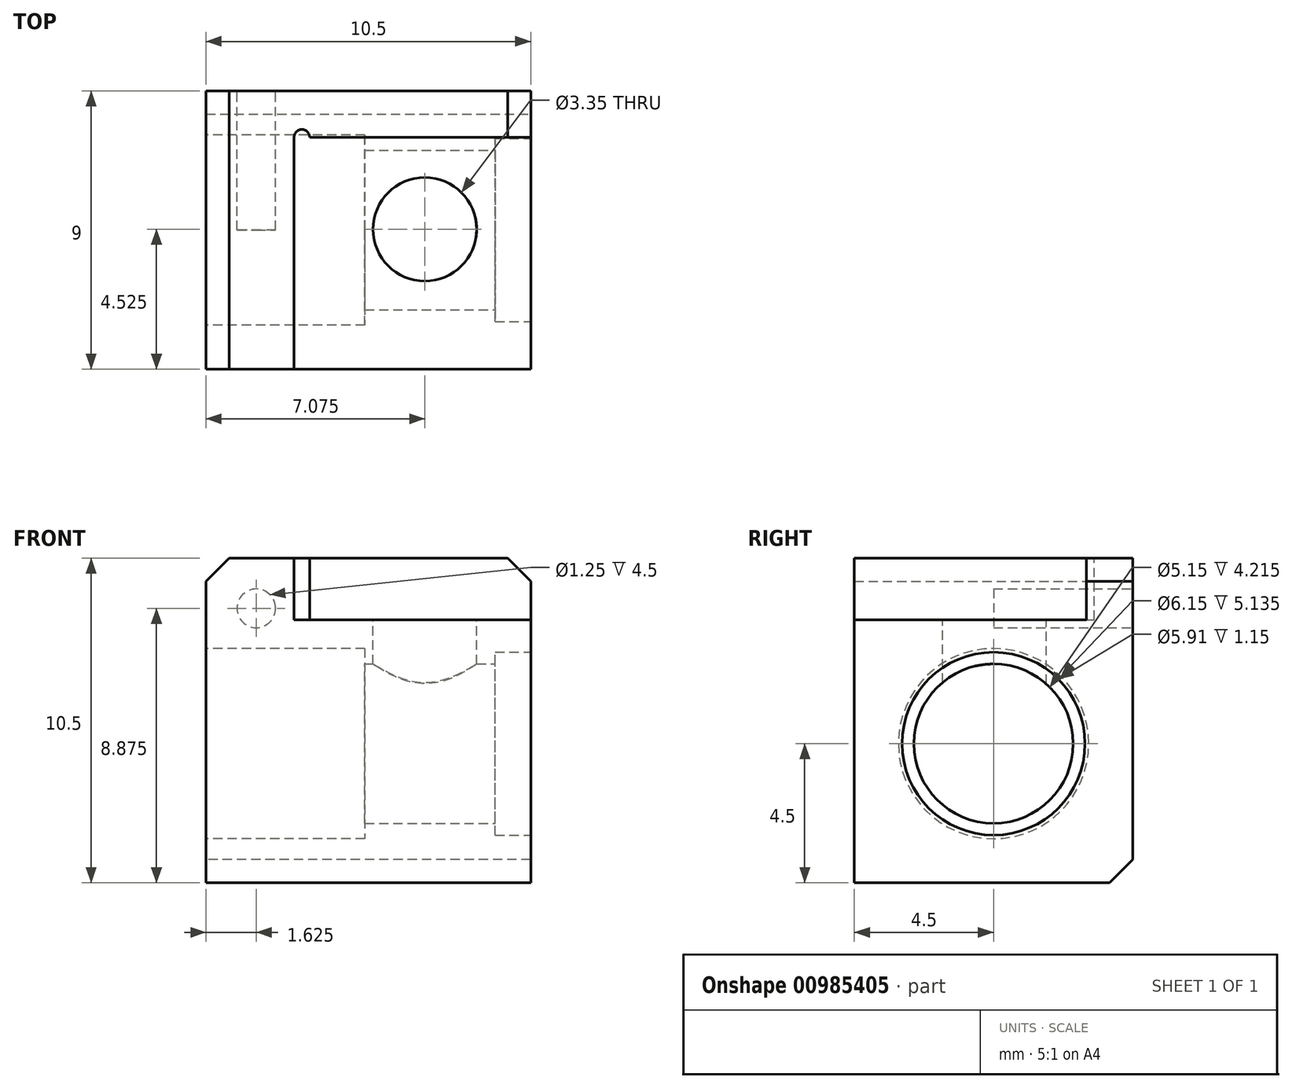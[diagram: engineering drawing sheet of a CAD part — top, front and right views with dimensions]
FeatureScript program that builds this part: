
annotation { "Feature Type Name" : "Feature", "Feature Type Description" : "" }
export const myFeature = defineFeature(function(context is Context, id is Id, definition is map)
    precondition{}
    {
        {
            var Q0;
            Q0=qCreatedBy(makeId("Front.planeOp"),FACE);
            var sketch = newSketch(context, id + "F0", { "sketchPlane" : qUnion([Q0])});
            skLineSegment(sketch, "E0.bottom", {"start": v(0, 0) * mm, "end": v(10.5, 0) * mm});
            skLineSegment(sketch, "E0.top", {"start": v(0, 10.5) * mm, "end": v(10.5, 10.5) * mm});
            skLineSegment(sketch, "E0.left", {"start": v(0, 0) * mm, "end": v(0, 10.5) * mm});
            skLineSegment(sketch, "E0.right", {"start": v(10.5, 0) * mm, "end": v(10.5, 10.5) * mm});
            skSolve(sketch);
        }
        {
            var Q0;
            Q0 = qSketchRegion(id + "F0", true);
            extrude(context, id + "F1", {"entities" : qUnion([Q0]), "depth" : 9 * mm, "offsetDistance" : 25.4 * mm});
        }
        {
            var Q0;
            Q0=makeQuery(id+"F1.opExtrude","SWEPT_FACE",FACE,{"disambiguationData":[OSD([sQuery(id+"F0.wireOp",EDGE,"E0.left")])]});
            var sketch = newSketch(context, id + "F2", { "sketchPlane" : qUnion([Q0])});
            skCircle(sketch, "E1", {"center": v(4.5, 4.5) * mm, "radius": 3.08 * mm});
            skPoint(sketch, "E1.centerSnap0", {"position": v(4.5, 0) * mm});
            skSolve(sketch);
        }
        {
            var Q0;
            Q0=makeQuery(id+"F2.imprint","IMPRINT",FACE,{"disambiguationData":[TD([[makeQuery(id+"F2.imprint","IMPRINT",EDGE,{"derivedFrom":sQuery(id+"F2.wireOp",EDGE,"E1")}),1.0]])]});
            extrude(context, id + "F3", {"entities" : qUnion([Q0]), "operationType" : NewBodyOperationType.REMOVE, "oppositeDirection" : true, "depth" : 5.13 * mm, "offsetDistance" : 25.4 * mm});
        }
        {
            var Q0;
            Q0=makeQuery(id+"F1.opExtrude","SWEPT_FACE",FACE,{"disambiguationData":[OSD([sQuery(id+"F0.wireOp",EDGE,"E0.right")])]});
            var sketch = newSketch(context, id + "F4", { "sketchPlane" : qUnion([Q0])});
            skCircle(sketch, "E2", {"center": v(-4.5, 4.5) * mm, "radius": 2.58 * mm});
            skPoint(sketch, "E2.centerSnap0", {"position": v(-4.5, 0) * mm});
            skSolve(sketch);
        }
        {
            var Q0;
            Q0 = qSketchRegion(id + "F4", true);
            extrude(context, id + "F5", {"entities" : qUnion([Q0]), "operationType" : NewBodyOperationType.REMOVE, "oppositeDirection" : true, "depth" : 25.4 * mm, "offsetDistance" : 25.4 * mm});
        }
        {
            var Q0;
            Q0=makeQuery(id+"F1.opExtrude","SWEPT_FACE",FACE,{"disambiguationData":[OSD([sQuery(id+"F0.wireOp",EDGE,"E0.top")])]});
            var sketch = newSketch(context, id + "F6", { "sketchPlane" : qUnion([Q0])});
            skLineSegment(sketch, "E3.bottom", {"start": v(10.5, -9) * mm, "end": v(2.85, -9) * mm});
            skLineSegment(sketch, "E3.top", {"start": v(10.5, -1.5) * mm, "end": v(2.85, -1.5) * mm});
            skLineSegment(sketch, "E3.left", {"start": v(10.5, -9) * mm, "end": v(10.5, -1.5) * mm});
            skLineSegment(sketch, "E3.right", {"start": v(2.85, -9) * mm, "end": v(2.85, -1.5) * mm});
            skCircle(sketch, "E4", {"center": v(3.1, -1.5) * mm, "radius": 0.25 * mm});
            skSolve(sketch);
        }
        {
            var Q0;
            Q0 = qSketchRegion(id + "F6", true);
            extrude(context, id + "F7", {"entities" : qUnion([Q0]), "operationType" : NewBodyOperationType.REMOVE, "oppositeDirection" : true, "depth" : 2 * mm, "offsetDistance" : 25.4 * mm});
        }
        {
            var Q0;
            Q0=makeQuery(id+"F7.boolean.opBoolean","COPY",FACE,{"derivedFrom":makeQuery(id+"F7.opExtrude","CAP_FACE",FACE,{"disambiguationData":[OSD([sQuery(id+"F6.wireOp",EDGE,"E3.bottom"),sQuery(id+"F6.wireOp",EDGE,"E3.top"),sQuery(id+"F6.wireOp",EDGE,"E3.left"),sQuery(id+"F6.wireOp",EDGE,"E3.right"),sQuery(id+"F6.wireOp",EDGE,"E4")])],"isStart":false})});
            var sketch = newSketch(context, id + "F8", { "sketchPlane" : qUnion([Q0])});
            skCircle(sketch, "E5", {"center": v(7.08, -4.48) * mm, "radius": 1.68 * mm});
            skSolve(sketch);
        }
        {
            var Q0;
            Q0 = qSketchRegion(id + "F8", true);
            extrude(context, id + "F9", {"entities" : qUnion([Q0]), "operationType" : NewBodyOperationType.REMOVE, "oppositeDirection" : true, "depth" : 3 * mm, "offsetDistance" : 25.4 * mm});
        }
        {
            var Q0;
            Q0=makeQuery(id+"F1.opExtrude","SWEPT_EDGE",EDGE,{"disambiguationData":[OSD([sQuery(id+"F0.wireOp",EDGE,"E0.top"),sQuery(id+"F0.wireOp",EDGE,"E0.left")])]});
            var Q1;
            Q1=makeQuery(id+"F1.opExtrude","CAP_EDGE",EDGE,{"disambiguationData":[OSD([sQuery(id+"F0.wireOp",EDGE,"E0.bottom")])],"isStart":true});
            var Q2;
            Q2=makeQuery(id+"F1.opExtrude","SWEPT_EDGE",EDGE,{"disambiguationData":[OSD([sQuery(id+"F0.wireOp",EDGE,"E0.top"),sQuery(id+"F0.wireOp",EDGE,"E0.right")])]});
            chamfer(context, id + "F10", {"entities" : qUnion([Q0, Q1, Q2]), "width" : .75 * mm, "tangentPropagation" : true});
        }
        {
            var Q0;
            Q0=makeQuery(id+"F1.opExtrude","CAP_FACE",FACE,{"disambiguationData":[OSD([sQuery(id+"F0.wireOp",EDGE,"E0.bottom"),sQuery(id+"F0.wireOp",EDGE,"E0.top"),sQuery(id+"F0.wireOp",EDGE,"E0.left"),sQuery(id+"F0.wireOp",EDGE,"E0.right")])],"isStart":true});
            var sketch = newSketch(context, id + "F11", { "sketchPlane" : qUnion([Q0])});
            skCircle(sketch, "E6", {"center": v(-1.63, 8.88) * mm, "radius": 0.62 * mm});
            skSolve(sketch);
        }
        {
            var Q0;
            Q0 = qSketchRegion(id + "F11", true);
            extrude(context, id + "F12", {"entities" : qUnion([Q0]), "operationType" : NewBodyOperationType.REMOVE, "oppositeDirection" : true, "depth" : 4.5 * mm, "offsetDistance" : 25.4 * mm});
        }
        {
            var Q0;
            Q0=makeQuery(id+"F1.opExtrude","SWEPT_FACE",FACE,{"disambiguationData":[OSD([sQuery(id+"F0.wireOp",EDGE,"E0.right")])]});
            var sketch = newSketch(context, id + "F13", { "sketchPlane" : qUnion([Q0])});
            skCircle(sketch, "E7", {"center": v(-4.5, 4.5) * mm, "radius": 2.96 * mm});
            skSolve(sketch);
        }
        {
            var Q0;
            Q0 = qSketchRegion(id + "F13", true);
            extrude(context, id + "F14", {"entities" : qUnion([Q0]), "operationType" : NewBodyOperationType.REMOVE, "oppositeDirection" : true, "depth" : 1.15 * mm, "offsetDistance" : 25.4 * mm});
        }
    });
